# Revit family: O19051001_Lavamanos Cascade Petite de Incrustar
name_source: partatom
category: Plumbing Fixtures
units: mm (PartAtom-declared; Revit-internal decimal feet)

## family parameters
Always vertical = Yes
Cut with Voids When Loaded = No
OmniClass Number = 23.31.13.11
OmniClass Title = Single Sinks
Part Type = Normal
Room Calculation Point = No
Round Connector Dimension = Use Diameter
Shared = No
Work Plane-Based = No

## types (1)
- Ref. O19051001 Lavamanos de incrustar en porcelana sanitaria
    Alto = 194 mm  [stored 0.636483 ft]
    Altura de instalación = 31,1” (79 cm)
    Ancho = 437 mm  [stored 1.43373 ft]
    Creado por = IDD
    Description = La línea Cascade nace a partir de la propuesta de CORONA de entregar un diseño amigable
y sorprendente, que busca facilitar la tareas y funciones del espacio del baño a nuestros
consumidores, su diseño se inspira en la caída del agua, por lo tanto, su forma es fluida,
pero con una mezcla de robustez que hace de la línea CASCADE un producto funcional,
pero a la vez resistente brindando mayor comodidad en su uso.
Los lavamanos de incrusta de esta linea se caracterizan por su diseño ovalado rectangular,
lo que lo hace de mayor capacidad, brindando mayor funcionalidad en su uso cotidiano, su
profundidad de 19cm facilita las actividades del diario minimizando el salpique.
• Tecnología AQUAFLOW魝〈, Superficie homogénea que impide la acumulación de agua y residuos.
• Tecnología COVERGLOSS魝〈, alta resistencia al rayado y a cambios de temperatura.
• Agujero integral que evita rebose.
• Acabado uniforme.
    Diametro del desagüe = 1,7” (4,3 cm)
    Dimensiones generales del pozo = 5,5” x 12,5” x 15,5” (14,1 cm x 32 cm x 396 cm)
    Dimensiones generales del producto = 7,6” x 14,3” x 17,2” (19,4 cm x 36,4 cm x 43,7 cm)
    Dimensiones generales del producto empacado = 8,3” x 15,2” x 17,9” (21,2 cm x 38,8 cm x 45,6 cm)
    Fecha de creación = 24/07/2020
    Manufacturer = Corona
    Material = Corona_Porcelana_Sanitaria
    Peso Bruto aprox = 18,9 Lb (8,6 kg)
    Peso Neto aprox = 17,6 Lb (8 kg)
    Profundidad = 364 mm  [stored 1.19423 ft]

note: [stored X ft] marks values corroborated as IEEE doubles in the binary element streams (Revit-internal decimal feet)

## geometry (parser evidence)
native form markers: Sweep x5
no freeform markers — native parametric forms only
